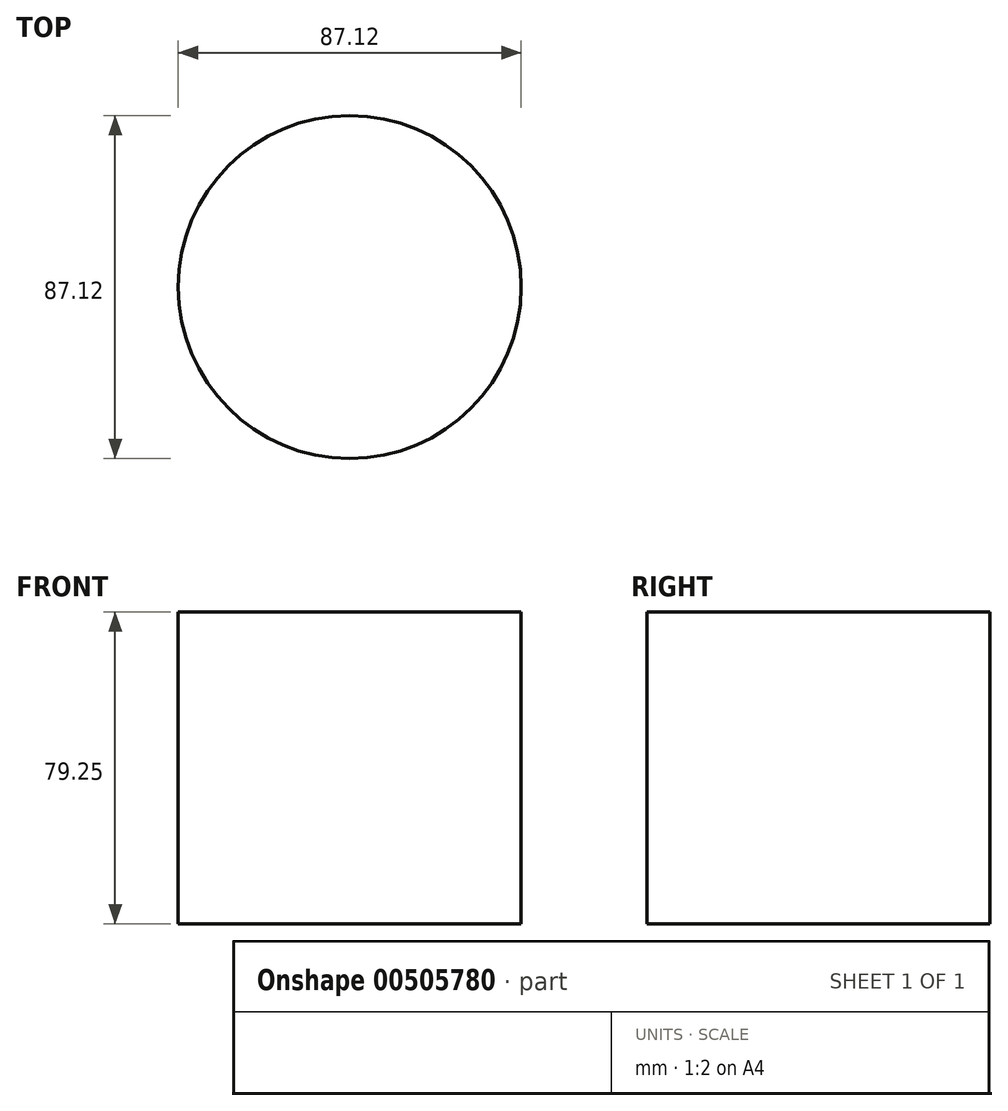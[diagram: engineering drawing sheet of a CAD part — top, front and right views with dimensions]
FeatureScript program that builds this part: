
annotation { "Feature Type Name" : "Feature", "Feature Type Description" : "" }
export const myFeature = defineFeature(function(context is Context, id is Id, definition is map)
    precondition{}
    {
        {
            var Q0;
            Q0=qCreatedBy(makeId("Top.planeOp"),FACE);
            var sketch = newSketch(context, id + "F0", { "sketchPlane" : qUnion([Q0])});
            skCircle(sketch, "E0", {"center": v(0, 0) * mm, "radius": 43.56 * mm});
            skSolve(sketch);
        }
        {
            var Q0;
            Q0 = qSketchRegion(id + "F0", true);
            extrude(context, id + "F1", {"entities" : qUnion([Q0]), "depth" : 79.25 * mm});
        }
    });
